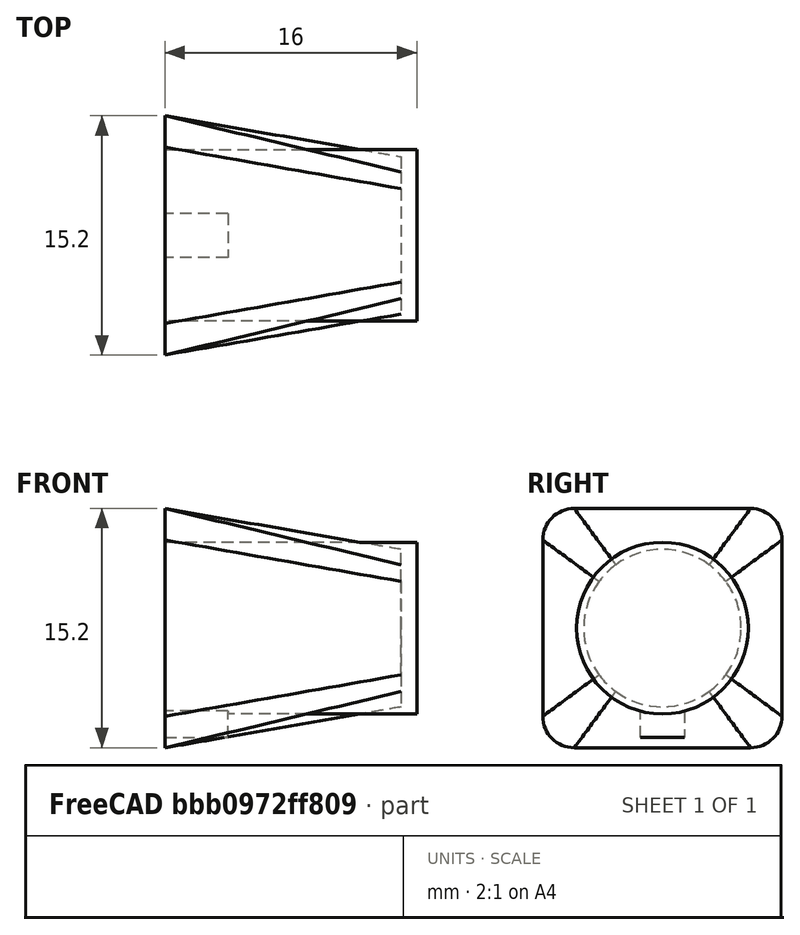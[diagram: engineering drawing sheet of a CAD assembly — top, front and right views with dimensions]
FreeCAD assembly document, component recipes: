
FREECAD ASSEMBLY — COMPONENT RECIPES ("abu-mount")

This assembly document has 2 components, labeled P0..P1 below (a component is one placed body or linked part). 2 of them carry a construction recipe — the FreeCAD feature program that regenerates the part from scratch, quoted from this document or its linked companion documents; the rest are supplied as boundary geometry only. No exploded tour is included for this assembly.
COMPONENT P0 — recipe-attached ("Connector001", modeled in this document).
Construction recipe (the document's own serialized feature program — sketch geometry with constraints, then the solid features built on it; lengths are millimeters unless a unit is written):

FEATURE [Sketcher::SketchObject] Sketch002  label="Start001"
  ArcFitTolerance = 1e-06
  FullyConstrained = true
  MakeInternals = false
  MapMode = 5
  Placement = pos=(0,0,0) rot=(0.57735,0.57735,0.57735;2.0944rad)
  sketch-geometry (8):
    g0: LineSegment StartX=-7.6 StartY=-5.6 StartZ=0 EndX=-7.6 EndY=5.6 EndZ=0
    g1: ArcOfCircle CenterX=-5.6 CenterY=5.6 CenterZ=0 NormalX=0 NormalY=0 NormalZ=1 AngleXU=0 Radius=2 StartAngle=1.5708 EndAngle=3.14159
    g2: LineSegment StartX=-5.6 StartY=7.6 StartZ=0 EndX=5.6 EndY=7.6 EndZ=0
    g3: ArcOfCircle CenterX=5.6 CenterY=5.6 CenterZ=0 NormalX=0 NormalY=0 NormalZ=1 AngleXU=0 Radius=2 StartAngle=2e-16 EndAngle=1.5708
    g4: LineSegment StartX=7.6 StartY=5.6 StartZ=0 EndX=7.6 EndY=-5.6 EndZ=0
    g5: ArcOfCircle CenterX=5.6 CenterY=-5.6 CenterZ=0 NormalX=0 NormalY=0 NormalZ=1 AngleXU=0 Radius=2 StartAngle=4.71239 EndAngle=6.28319
    g6: LineSegment StartX=5.6 StartY=-7.6 StartZ=0 EndX=-5.6 EndY=-7.6 EndZ=0
    g7: ArcOfCircle CenterX=-5.6 CenterY=-5.6 CenterZ=0 NormalX=0 NormalY=0 NormalZ=1 AngleXU=0 Radius=2 StartAngle=3.14159 EndAngle=4.71239
  constraints (19):
    c: Vertical(g0)
    c: Tangent(g0,g1) = 1.5708
    c: Tangent(g1,g2) = 1.5708
    c: Tangent(g2,g3) = 1.5708
    c: Tangent(g3,g4) = 1.5708
    c: Tangent(g4,g5) = 1.5708
    c: Tangent(g5,g6) = 1.5708
    c: Parallel(g2,g-1)
    c: Parallel(g6,g-1)
    c: Parallel(g4,g-2)
    c: Equal(g2,g4)
    c: Equal(g4,g6)
    c: Equal(g6,g0)
    c: Equal(g1,g3)
    c: Tangent(g7,g6) = 1.5708
    c: Tangent(g7,g0) = 1.5708
    c: Radius(g1) = 2
    c: DistanceX(g0,g3) = 15.2
    c: Symmetric(g3,g7,g-1)
FEATURE [Sketcher::SketchObject] Sketch005  label="End001"
  ArcFitTolerance = 1e-06
  FullyConstrained = true
  MakeInternals = false
  MapMode = 5
  Placement = pos=(15,0,0) rot=(0.57735,0.57735,0.57735;2.0944rad)
  sketch-geometry (1):
    g0: Circle CenterX=0 CenterY=0 CenterZ=0 NormalX=0 NormalY=0 NormalZ=1 AngleXU=0 Radius=5
  constraints (2):
    c: Coincident(g0,g-1)
    c: Diameter(g0) = 10
FEATURE [PartDesign::AdditiveLoft] AdditiveLoft
  Closed = false
  Placement = pos=(0,0,0) rot=(0.57735,0.57735,0.57735;2.0944rad)
  Profile = -> Sketch002
  Refine = true
  Ruled = false
  Sections = -> [Sketch005]
  Suppressed = false
FEATURE [PartDesign::Body] Body002  label="Connector"
  AllowCompound = false
  Group = -> [Sketch002,Sketch005,AdditiveLoft]
  Origin = -> Origin003
  Tip = -> AdditiveLoft
COMPONENT P1 — recipe-attached ("Shaft001", modeled in this document).
Construction recipe (the document's own serialized feature program — sketch geometry with constraints, then the solid features built on it; lengths are millimeters unless a unit is written):

FEATURE [Sketcher::SketchObject] Sketch006  label="Cylinder"
  ArcFitTolerance = 1e-06
  AttachmentSupport = -> [YZ_Plane004]
  FullyConstrained = true
  MakeInternals = false
  MapMode = 5
  Placement = pos=(0,0,0) rot=(0.57735,0.57735,0.57735;2.0944rad)
  sketch-geometry (1):
    g0: Circle CenterX=0 CenterY=0 CenterZ=0 NormalX=0 NormalY=0 NormalZ=1 AngleXU=0 Radius=5.45
  constraints (2):
    c: Coincident(g0,g-1)
    c: Diameter(g0) = 10.9
FEATURE [PartDesign::Pad] Pad001
  Direction = (1,0,0)
  Length = 16
  Length2 = 10
  Placement = pos=(0,0,0) rot=(1,1,1;2.0944rad)
  Profile = -> Sketch006
  ReferenceAxis = -> Sketch006 [N_Axis]
  Refine = true
  Suppressed = false
  Type = 0
FEATURE [Sketcher::SketchObject] Sketch007
  ArcFitTolerance = 1e-06
  AttachmentSupport = -> [YZ_Plane004]
  FullyConstrained = true
  MakeInternals = false
  MapMode = 5
  Placement = pos=(0,0,0) rot=(0.57735,0.57735,0.57735;2.0944rad)
  sketch-geometry (5):
    g0: LineSegment StartX=-1.4 StartY=0 StartZ=0 EndX=1.4 EndY=0 EndZ=0
    g1: LineSegment StartX=1.4 StartY=0 StartZ=0 EndX=1.4 EndY=-6.95 EndZ=0
    g2: LineSegment StartX=1.4 StartY=-6.95 StartZ=0 EndX=-1.4 EndY=-6.95 EndZ=0
    g3: LineSegment StartX=-1.4 StartY=-6.95 StartZ=0 EndX=-1.4 EndY=0 EndZ=0
    g4: LineSegment [constr] StartX=0 StartY=0 StartZ=0 EndX=0 EndY=-5.45 EndZ=0
  constraints (13):
    c: Coincident(g0,g1)
    c: Coincident(g1,g2)
    c: Coincident(g2,g3)
    c: Coincident(g3,g0)
    c: Horizontal(g0)
    c: Vertical(g1)
    c: DistanceX(g2,g2) = 2.8
    c: Symmetric(g2,g1,g-2)
    c: Coincident(g4,g-1)
    c: PointOnObject(g4,g-2)
    c: DistanceY(g4,g4) = 5.45
    c: DistanceY(g1,g4) = 1.5
    c: Symmetric(g0,g0,g4)
FEATURE [PartDesign::Pad] Pad002  label="Rotation Lock"
  BaseFeature = -> Pad001
  Direction = (1,0,0)
  Length = 4
  Length2 = 10
  Placement = pos=(0,0,0) rot=(1,1,1;2.0944rad)
  Profile = -> Sketch007
  ReferenceAxis = -> Sketch007 [N_Axis]
  Refine = true
  Suppressed = false
  Type = 0
FEATURE [PartDesign::Body] Body003  label="Shaft"
  AllowCompound = false
  Group = -> [Sketch006,Pad001,Sketch007,Pad002]
  Origin = -> Origin004
  Tip = -> Pad002
PROVENANCE & LICENSES
A FreeCAD (.FCStd) document from a public repository crawl; recipes are the document's own serialized feature recipes (and, for linked parts, companion documents' recipes).
License: as declared in the source repository (recorded in the dataset sidecar).
